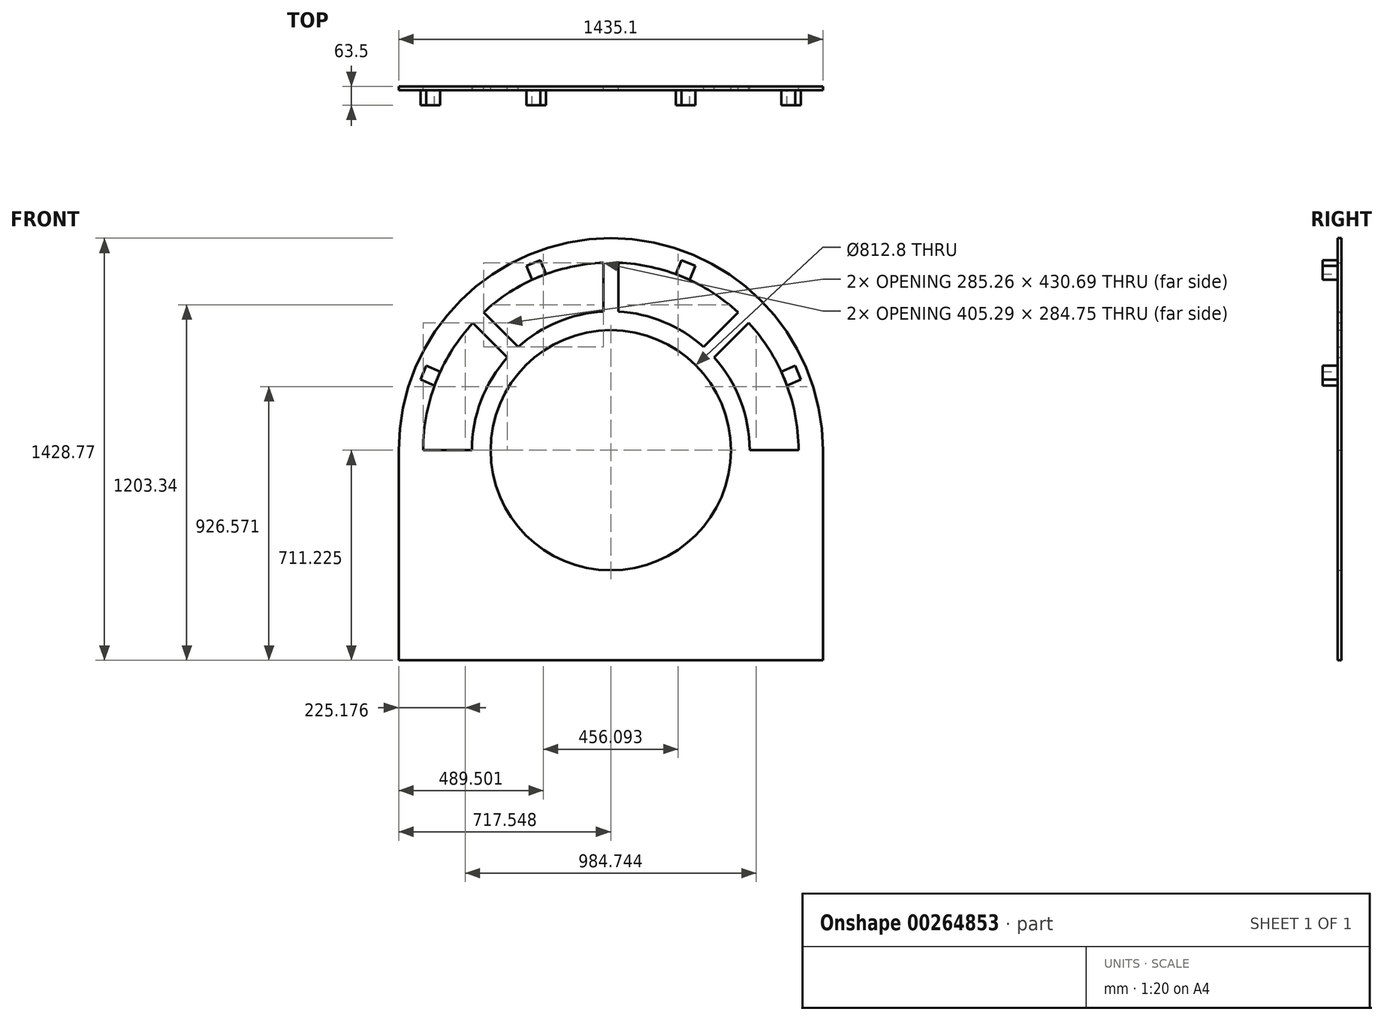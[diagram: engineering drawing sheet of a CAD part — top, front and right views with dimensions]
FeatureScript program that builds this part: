
annotation { "Feature Type Name" : "Feature", "Feature Type Description" : "" }
export const myFeature = defineFeature(function(context is Context, id is Id, definition is map)
    precondition{}
    {
        {
            var Q0;
            Q0=qCreatedBy(makeId("Front.planeOp"),FACE);
            var sketch = newSketch(context, id + "F0", { "sketchPlane" : qUnion([Q0])});
            skCircle(sketch, "E0", {"center": v(-95.1, -133.03) * mm, "radius": 406.4 * mm});
            skArc(sketch, "E1", {"start": v(622.45, -133.03) * mm, "mid": v(-95.1, 584.52) * mm, "end": v(-812.65, -133.03) * mm});
            skPoint(sketch, "E2.center", {"position": v(0, 0) * mm});
            skLineSegment(sketch, "E3", {"start": v(0, -844.25) * mm, "end": v(-812.65, -844.25) * mm});
            skLineSegment(sketch, "E4", {"start": v(0, -844.25) * mm, "end": v(622.45, -844.25) * mm});
            skLineSegment(sketch, "E5", {"start": v(-565, -133.03) * mm, "end": v(-730.1, -133.03) * mm});
            skLineSegment(sketch, "E6", {"start": v(-812.65, -133.03) * mm, "end": v(-812.65, -844.25) * mm});
            skLineSegment(sketch, "E7", {"start": v(622.45, -133.03) * mm, "end": v(622.45, -844.25) * mm});
            skArc(sketch, "E8", {"start": v(539.9, -133.03) * mm, "mid": v(496.3, 98.2) * mm, "end": v(371.51, 297.67) * mm});
            skArc(sketch, "E9", {"start": v(374.8, -133.03) * mm, "mid": v(343.73, 35) * mm, "end": v(254.64, 180.8) * mm});
            skLineSegment(sketch, "E10.trimOffspring", {"start": v(374.8, -133.03) * mm, "end": v(539.9, -133.03) * mm});
            skPoint(sketch, "E11.center", {"position": v(0, -133.03) * mm});
            skArc(sketch, "E12.trimOffspring", {"start": v(-561.72, 297.67) * mm, "mid": v(-686.5, 98.2) * mm, "end": v(-730.1, -133.03) * mm});
            skArc(sketch, "E13.trimOffspring", {"start": v(-444.85, 180.8) * mm, "mid": v(-533.94, 35) * mm, "end": v(-565, -133.03) * mm});
            skArc(sketch, "E14.trimOffspring", {"start": v(-120.5, 501.47) * mm, "mid": v(-338.1, 453.64) * mm, "end": v(-525.8, 333.59) * mm});
            skLineSegment(sketch, "E15", {"start": v(-120.5, 501.47) * mm, "end": v(-120.5, 336.19) * mm});
            skLineSegment(sketch, "E16", {"start": v(-69.7, 501.47) * mm, "end": v(-69.7, 336.19) * mm});
            skArc(sketch, "E17.trimOffspring", {"start": v(-120.5, 336.19) * mm, "mid": v(-274.93, 301.1) * mm, "end": v(-408.93, 216.72) * mm});
            skLineSegment(sketch, "E18.1.0", {"start": v(-561.72, 297.67) * mm, "end": v(-444.85, 180.8) * mm});
            skLineSegment(sketch, "E18.1.1", {"start": v(-525.8, 333.59) * mm, "end": v(-408.93, 216.72) * mm});
            skLineSegment(sketch, "E18.7.0", {"start": v(335.6, 333.59) * mm, "end": v(218.72, 216.72) * mm});
            skLineSegment(sketch, "E18.7.1", {"start": v(371.51, 297.67) * mm, "end": v(254.64, 180.8) * mm});
            skArc(sketch, "E19.trimOffspring", {"start": v(335.6, 333.59) * mm, "mid": v(147.9, 453.64) * mm, "end": v(-69.7, 501.47) * mm});
            skArc(sketch, "E20.trimOffspring", {"start": v(218.72, 216.72) * mm, "mid": v(84.72, 301.1) * mm, "end": v(-69.7, 336.19) * mm});
            skLineSegment(sketch, "E21", {"start": v(-95.1, -133.03) * mm, "end": v(498.36, 460.44) * mm});
            skLineSegment(sketch, "E22", {"start": v(-95.1, 570.27) * mm, "end": v(-95.1, -133.03) * mm});
            skLineSegment(sketch, "E23", {"start": v(-95.1, -133.03) * mm, "end": v(-685.22, 457.1) * mm});
            skSolve(sketch);
        }
        {
            var Q0;
            Q0=makeQuery(id+"F0.imprint","IMPRINT",FACE,{"disambiguationData":[TD([[makeQuery(id+"F0.imprint","IMPRINT",EDGE,{"derivedFrom":sQuery(id+"F0.wireOp",EDGE,"E0")}),-1.0]])]});
            var Q1;
            {var subQ0=sQuery(id+"F0.wireOp",EDGE,"tCiKNfFr-cMDh-xXLL-zOdQ-TLV0AaxXYuFO");Q1=makeQuery(id+"F0.imprint","IMPRINT",FACE,{"disambiguationData":[TD([[makeQuery(id+"F0.imprint","IMPRINT",EDGE,{"derivedFrom":subQ0}),-1.0]])]});}
            var Q2;
            {var subQ0=sQuery(id+"F0.wireOp",EDGE,"w7s3Jzrb-C9Dm-h4AE-YciC-SPQUsxUZpe8J");Q2=makeQuery(id+"F0.imprint","IMPRINT",FACE,{"disambiguationData":[TD([[makeQuery(id+"F0.imprint","IMPRINT",EDGE,{"derivedFrom":subQ0}),-1.0]])]});}
            var Q3;
            {var subQ0=sQuery(id+"F0.wireOp",EDGE,"E4");Q3=makeQuery(id+"F0.imprint","IMPRINT",FACE,{"disambiguationData":[TD([[makeQuery(id+"F0.imprint","IMPRINT",EDGE,{"derivedFrom":subQ0}),1.0]])]});}
            var Q4;
            {var subQ0=sQuery(id+"F0.wireOp",EDGE,"E3");Q4=makeQuery(id+"F0.imprint","IMPRINT",FACE,{"disambiguationData":[TD([[makeQuery(id+"F0.imprint","IMPRINT",EDGE,{"derivedFrom":subQ0}),-1.0]])]});}
            extrude(context, id + "F1", {"entities" : qUnion([Q0, Q1, Q2, Q3, Q4]), "depth" : 12.7 * mm});
        }
        {
            var Q0;
            Q0=makeQuery(id+"F1.opExtrude","CAP_FACE",FACE,{"disambiguationData":[OSD([sQuery(id+"F0.wireOp",EDGE,"E0"),sQuery(id+"F0.wireOp",EDGE,"E1"),sQuery(id+"F0.wireOp",EDGE,"E3"),sQuery(id+"F0.wireOp",EDGE,"E4"),sQuery(id+"F0.wireOp",EDGE,"E5"),sQuery(id+"F0.wireOp",EDGE,"E6"),sQuery(id+"F0.wireOp",EDGE,"E7"),sQuery(id+"F0.wireOp",EDGE,"E8"),sQuery(id+"F0.wireOp",EDGE,"E9"),sQuery(id+"F0.wireOp",EDGE,"E10.trimOffspring"),sQuery(id+"F0.wireOp",EDGE,"E12.trimOffspring"),sQuery(id+"F0.wireOp",EDGE,"E13.trimOffspring"),sQuery(id+"F0.wireOp",EDGE,"E14.trimOffspring"),sQuery(id+"F0.wireOp",EDGE,"E15"),sQuery(id+"F0.wireOp",EDGE,"E16"),sQuery(id+"F0.wireOp",EDGE,"E17.trimOffspring"),sQuery(id+"F0.wireOp",EDGE,"E18.1.0"),sQuery(id+"F0.wireOp",EDGE,"E18.1.1"),sQuery(id+"F0.wireOp",EDGE,"E18.7.0"),sQuery(id+"F0.wireOp",EDGE,"E18.7.1"),sQuery(id+"F0.wireOp",EDGE,"E19.trimOffspring"),sQuery(id+"F0.wireOp",EDGE,"E20.trimOffspring")])],"isStart":false});
            var sketch = newSketch(context, id + "F2", { "sketchPlane" : qUnion([Q0])});
            skLineSegment(sketch, "E24", {"start": v(-95.1, -133.03) * mm, "end": v(-681.77, 109.98) * mm});
            skLineSegment(sketch, "E25", {"start": v(-95.1, -133.03) * mm, "end": v(-95.1, 541.97) * mm});
            skLineSegment(sketch, "E26", {"start": v(-95.1, -133.03) * mm, "end": v(-646.7, 418.56) * mm});
            skLineSegment(sketch, "E27", {"start": v(-738.42, 105.95) * mm, "end": v(-718.98, 152.89) * mm});
            skLineSegment(sketch, "E28", {"start": v(-718.98, 152.89) * mm, "end": v(-672.05, 133.45) * mm});
            skLineSegment(sketch, "E29", {"start": v(-672.05, 133.45) * mm, "end": v(-691.49, 86.51) * mm});
            skLineSegment(sketch, "E30", {"start": v(-691.49, 86.51) * mm, "end": v(-738.42, 105.95) * mm});
            skCircle(sketch, "E31", {"center": v(-95.1, -133.03) * mm, "radius": 311.85 * mm});
            skLineSegment(sketch, "E32.1.0", {"start": v(-361.57, 443.92) * mm, "end": v(-381.01, 490.85) * mm});
            skLineSegment(sketch, "E32.1.1", {"start": v(-314.64, 463.36) * mm, "end": v(-361.57, 443.92) * mm});
            skLineSegment(sketch, "E32.1.2", {"start": v(-334.08, 510.3) * mm, "end": v(-314.64, 463.36) * mm});
            skLineSegment(sketch, "E32.1.3", {"start": v(-381.01, 490.85) * mm, "end": v(-334.08, 510.3) * mm});
            skLineSegment(sketch, "E32.2.0", {"start": v(124.44, 463.36) * mm, "end": v(143.88, 510.3) * mm});
            skLineSegment(sketch, "E32.2.1", {"start": v(171.37, 443.92) * mm, "end": v(124.44, 463.36) * mm});
            skLineSegment(sketch, "E32.2.2", {"start": v(190.8, 490.85) * mm, "end": v(171.37, 443.92) * mm});
            skLineSegment(sketch, "E32.2.3", {"start": v(143.88, 510.3) * mm, "end": v(190.8, 490.85) * mm});
            skLineSegment(sketch, "E32.3.0", {"start": v(481.84, 133.45) * mm, "end": v(528.77, 152.89) * mm});
            skLineSegment(sketch, "E32.3.1", {"start": v(501.28, 86.51) * mm, "end": v(481.84, 133.45) * mm});
            skLineSegment(sketch, "E32.3.2", {"start": v(548.21, 105.95) * mm, "end": v(501.28, 86.51) * mm});
            skLineSegment(sketch, "E32.3.3", {"start": v(528.77, 152.89) * mm, "end": v(548.21, 105.95) * mm});
            skLineSegment(sketch, "E32.anchor1", {"start": v(-95.1, -133.03) * mm, "end": v(-738.42, 105.95) * mm, "construction": true});
            skLineSegment(sketch, "E32.anchor2", {"start": v(-95.1, -133.03) * mm, "end": v(528.77, 152.89) * mm, "construction": true});
            skSolve(sketch);
        }
        {
            var Q0;
            Q0=makeQuery(id+"F2.imprint","IMPRINT",FACE,{"disambiguationData":[TD([[makeQuery(id+"F2.imprint","IMPRINT",EDGE,{"derivedFrom":sQuery(id+"F2.wireOp",EDGE,"E27")}),-1.0]])]});
            var Q1;
            Q1=makeQuery(id+"F2.imprint","IMPRINT",FACE,{"disambiguationData":[TD([[makeQuery(id+"F2.imprint","IMPRINT",EDGE,{"derivedFrom":sQuery(id+"F2.wireOp",EDGE,"E32.3.0")}),-1.0]])]});
            var Q2;
            Q2=makeQuery(id+"F2.imprint","IMPRINT",FACE,{"disambiguationData":[TD([[makeQuery(id+"F2.imprint","IMPRINT",EDGE,{"derivedFrom":sQuery(id+"F2.wireOp",EDGE,"E32.1.0")}),-1.0]])]});
            var Q3;
            Q3=makeQuery(id+"F2.imprint","IMPRINT",FACE,{"disambiguationData":[TD([[makeQuery(id+"F2.imprint","IMPRINT",EDGE,{"derivedFrom":sQuery(id+"F2.wireOp",EDGE,"E32.2.0")}),-1.0]])]});
            extrude(context, id + "F3", {"entities" : qUnion([Q0, Q1, Q2, Q3]), "operationType" : NewBodyOperationType.ADD, "depth" : 50.8 * mm, "offsetDistance" : 25.4 * mm});
        }
    });
